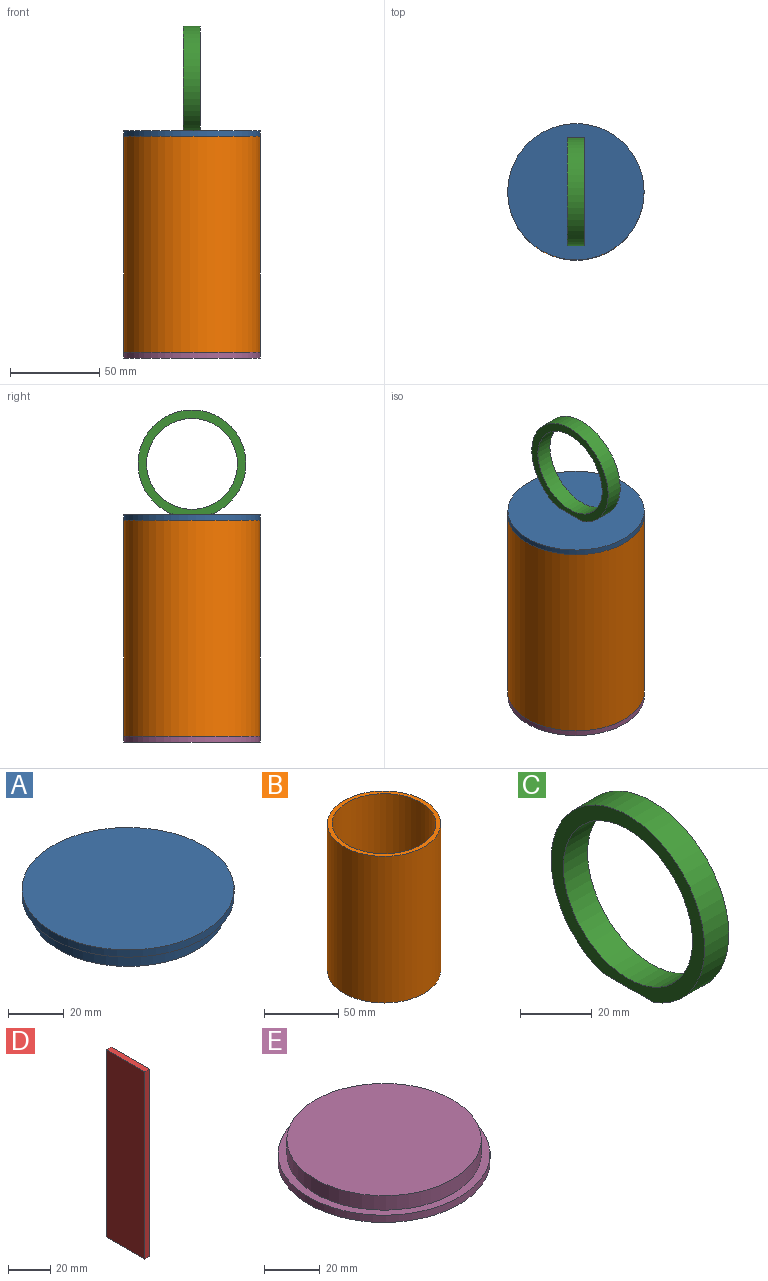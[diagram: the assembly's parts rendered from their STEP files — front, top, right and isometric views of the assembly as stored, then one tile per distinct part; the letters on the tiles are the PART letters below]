
ASSEMBLY  parts=5 mates=4
PART A: 5 faces, bbox 76.2x76.2x9.5 mm
  f0: plane 76.2x76.2mm, normal (0,0,1), area 4560.4mm2, adj f4
  f1: plane 69.85x69.85mm, normal (0,0,-1), area 3832mm2, adj f2
  f2: cylinder r=34.92mm len=69.85mm, axis (0,0,1), area 1393.4mm2, adj f1,f3
  f3: plane 76.2x76.2mm, normal (0,0,-1), area 728.4mm2, adj f2,f4
  f4: cylinder r=38.1mm len=76.2mm, axis (0,0,1), area 760.1mm2, adj f0,f3
PART B: 4 faces, bbox 76.2x76.2x120.7 mm
  f0: plane 76.2x76.2mm, normal (0,0,1), area 728.4mm2, adj f1,f2
  f1: cylinder r=34.92mm len=120.65mm, axis (0,0,-1), area 26475.5mm2, adj f0,f3
  f2: cylinder r=38.1mm len=120.65mm, axis (0,0,-1), area 28882.3mm2, adj f0,f3
  f3: plane 76.2x76.2mm, normal (0,0,-1), area 728.4mm2, adj f1,f2
PART C: 5 faces, bbox 9.5x60.3x58.6 mm
  f0: cylinder r=30.16mm len=60.33mm, axis (-1,0,0), area 1610.5mm2, adj f1,f2,f4
  f1: plane 60.33x58.61mm, normal (1,0,0), area 808.3mm2, adj f0,f3,f4
  f2: plane 60.33x58.61mm, normal (-1,0,0), area 808.3mm2, adj f0,f3,f4
  f3: cylinder r=25.4mm len=50.8mm, axis (-1,0,0), area 1520.1mm2, adj f1,f2
  f4: plane 20.05x9.53mm, normal (0,0,-1), area 191mm2, adj f0,f1,f2
PART D: 6 faces, bbox 3.2x25.4x108 mm
  f0: plane 25.4x3.18mm, normal (0,0,1), area 80.6mm2, adj f1,f3,f4,f5
  f1: plane 107.95x25.4mm, normal (-1,0,0), area 2741.9mm2, adj f0,f2,f3,f4
  f2: plane 25.4x3.18mm, normal (0,0,-1), area 80.6mm2, adj f1,f3,f4,f5
  f3: plane 107.95x3.18mm, normal (0,-1,0), area 342.7mm2, adj f0,f1,f2,f5
  f4: plane 107.95x3.18mm, normal (0,1,0), area 342.7mm2, adj f0,f1,f2,f5
  f5: plane 107.95x25.4mm, normal (1,0,0), area 2741.9mm2, adj f0,f2,f3,f4
PART E: 5 faces, bbox 76.2x76.2x9.5 mm
  f0: plane 76.2x76.2mm, normal (0,0,-1), area 4560.4mm2, adj f1
  f1: cylinder r=38.1mm len=76.2mm, axis (0,0,1), area 760.1mm2, adj f0,f2
  f2: plane 76.2x76.2mm, normal (0,0,1), area 728.4mm2, adj f1,f3
  f3: cylinder r=34.92mm len=69.85mm, axis (0,0,1), area 1393.4mm2, adj f2,f4
  f4: plane 69.85x69.85mm, normal (0,0,1), area 3832mm2, adj f3
PLACE A at identity
PLACE B at identity
PLACE C at identity
PLACE D at identity
PLACE E at identity fixed
MATE fastened B.f1 <-> E.f1  axis (0,0,-1) through (0,0,3.17)mm
MATE fastened E.f1 <-> D.f2  axis (0,0,1) through (0,0,9.53)mm
MATE fastened B.f1 <-> A.f2  axis (0,0,1) through (0,0,123.82)mm
MATE fastened A.f2 <-> C.f4  axis (0,0,1) through (0,0,127)mm
